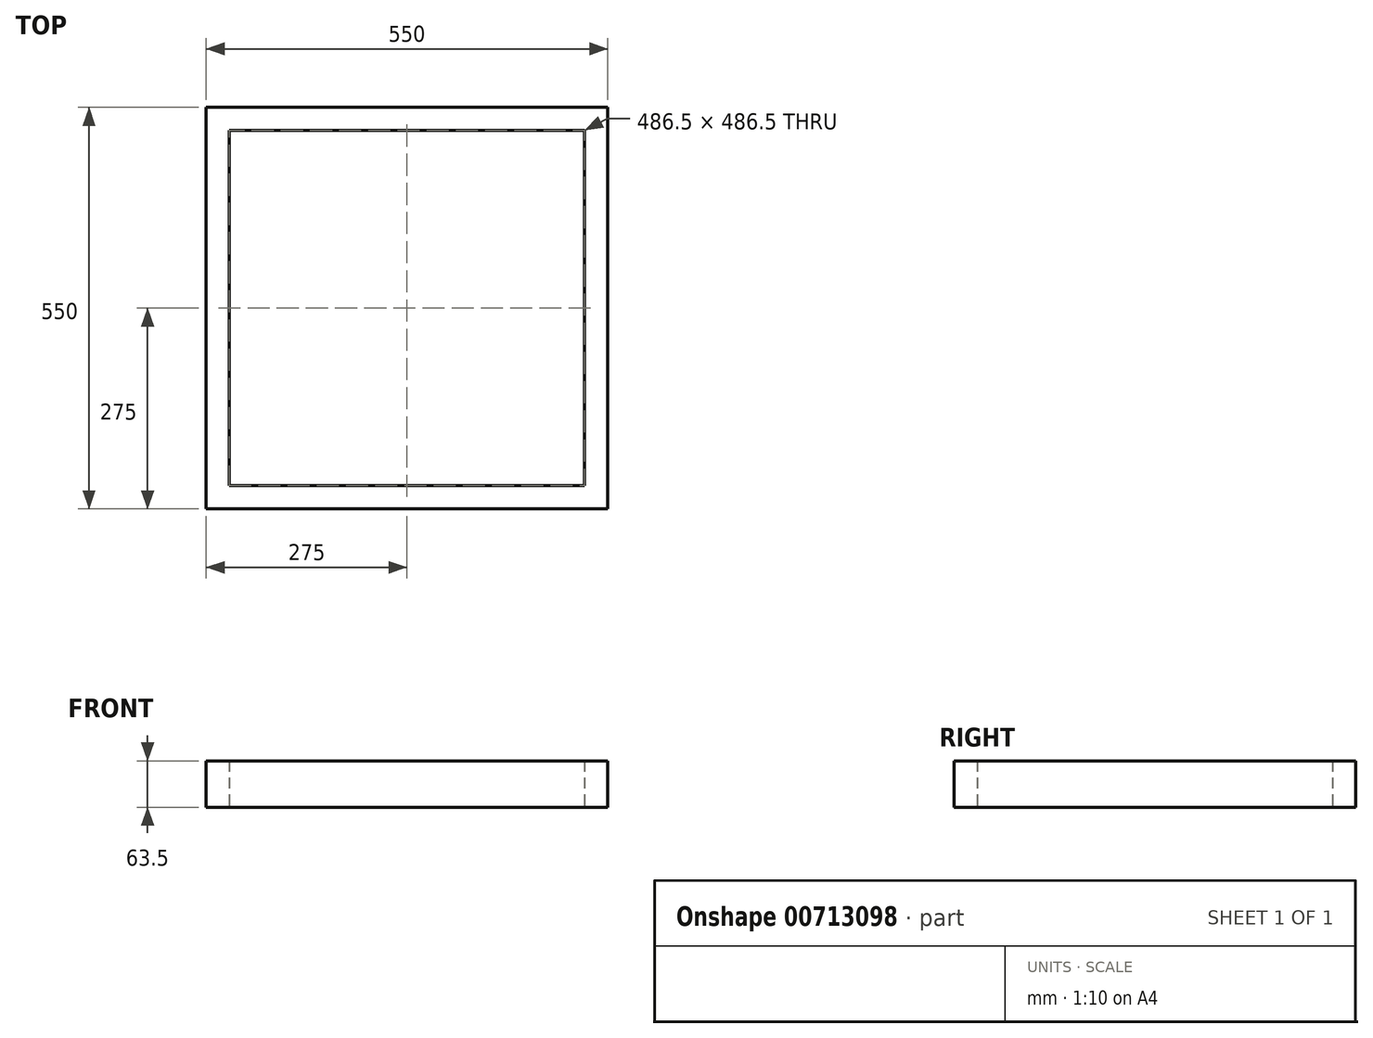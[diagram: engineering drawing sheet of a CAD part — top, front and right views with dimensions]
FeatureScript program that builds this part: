
annotation { "Feature Type Name" : "Feature", "Feature Type Description" : "" }
export const myFeature = defineFeature(function(context is Context, id is Id, definition is map)
    precondition{}
    {
        {
            var Q0;
            Q0=qCreatedBy(makeId("Top.planeOp"),FACE);
            var sketch = newSketch(context, id + "F0", { "sketchPlane" : qUnion([Q0])});
            skLineSegment(sketch, "E0.bottom", {"start": v(275, -275) * mm, "end": v(-275, -275) * mm});
            skLineSegment(sketch, "E0.top", {"start": v(275, 275) * mm, "end": v(-275, 275) * mm});
            skLineSegment(sketch, "E0.left", {"start": v(275, -275) * mm, "end": v(275, 275) * mm});
            skLineSegment(sketch, "E0.right", {"start": v(-275, -275) * mm, "end": v(-275, 275) * mm});
            skPoint(sketch, "E0.middle", {"position": v(0, 0) * mm});
            skLineSegment(sketch, "E1.bottom", {"start": v(243.25, -243.25) * mm, "end": v(-243.25, -243.25) * mm});
            skLineSegment(sketch, "E1.top", {"start": v(243.25, 243.25) * mm, "end": v(-243.25, 243.25) * mm});
            skLineSegment(sketch, "E1.left", {"start": v(243.25, -243.25) * mm, "end": v(243.25, 243.25) * mm});
            skLineSegment(sketch, "E1.right", {"start": v(-243.25, -243.25) * mm, "end": v(-243.25, 243.25) * mm});
            skSolve(sketch);
        }
        {
            var Q0;
            Q0=makeQuery(id+"F0.imprint","IMPRINT",FACE,{"disambiguationData":[TD([[makeQuery(id+"F0.imprint","IMPRINT",EDGE,{"derivedFrom":sQuery(id+"F0.wireOp",EDGE,"E0.bottom")}),-1.0]])]});
            extrude(context, id + "F1", {"entities" : qUnion([Q0]), "depth" : 63.5 * mm, "offsetDistance" : 25 * mm});
        }
    });
